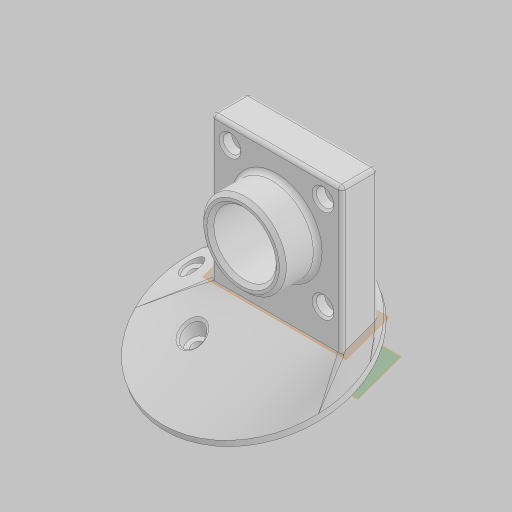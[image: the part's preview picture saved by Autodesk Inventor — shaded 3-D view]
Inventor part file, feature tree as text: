
AUTODESK INVENTOR PART (.ipt)
format: ipt  version: 2023.5 (Build 275446000, 446)  size: 464,384 bytes
history: native  units: in
note: dims shown in document units (in); Inventor stores cm internally (conversion verified against a paired STEP export)
features: extrude x7, hole x3, fillet x3, other x3, projected_geometry x3, plane x2, chamfer x2, loft x1, sketch x1, revolve x1
ambient origin geometry x8: Origin, YZ Plane, XZ Plane, XY Plane, X Axis, Y Axis, Z Axis, Center Point
bodies: Solid1 (feature_tree)
feature tree (26):
  extrude  "Extrusion1"  Depth=0.15in
  extrude  "Extrusion2"  Depth=0.15in TaperAngle=0.0deg
  plane  "Work Plane1"
  extrude  "Extrusion3"  Depth=0.15in
  loft  "Loft1"
  extrude  "Extrusion4"  Depth=0.15in
  hole  "Hole1"  [1 undecoded]
  extrude  "Extrusion5"  Depth=0.15in TaperAngle=0.0deg
  extrude  "Extrusion6"  TaperAngle=0.0deg  [1 undecoded]
  hole  "Hole2"  [1 undecoded]
  plane  "Work Plane2"
  hole  "Hole3"  [1 undecoded]
  fillet  "Fillet1"  Radius=0.3in
  chamfer  "Chamfer1"  Distance=1.1875in
  fillet  "Fillet2"  Radius=0.5in
  extrude  "Extrusion7"  Depth=0.15in
  fillet  "Fillet3"  Radius=1.3386in
  chamfer  "Chamfer2"  Distance=0.15in
  other  "Edges1"
  other  "Edges2"
  projected_geometry  "Projected Loop1"
  projected_geometry  "Projected Loop2"
  sketch  "Sketch11"  dims[d0=1.875in d1=0.525in d2=1.875in d3=0.0in d4=0.481in d5=1.875in d6=0.0in d7=0.6in d9=2.75in d10=0.1in d11=0.0in d12=0.0in d13=90.0deg d14=0.0in d15=90.0deg d16=1.6in d17=0.3in d18=0.0in d19=0.9in d20=0.75in d21=0.119in d22=0.25in d23=0.6871in d24=1.0in d25=0.8108in d26=1.1875in d27=0.5in d28=0.0in d29=0.1839in d30=1.3386in d31=0.15in d32=0.0in d33=0.094in d34=0.75in d35=0.251in d36=0.15in d37=0.6871in d38=1.0in d39=0.8108in d40=0.9792in d41=0.9792in d42=315.0deg d45=0.177in d46=0.75in d47=0.313in d48=0.45in d49=0.5635in d50=1.0in d51=0.8108in d52=0.05in d53=0.05in d54=0.125in d55=45.0deg d56=0.0625in d57=1.0in d58=1.0in d59=0.0in d60=0.25in d61=0.0312in d62=0.125in d63=45.0deg d64=0.2405in d65=90.0deg]
  other  "Srf1"
  revolve  "RevolutionSrf1"  [1 undecoded]
  projected_geometry  "Project Cut Edges1"
note: 5 required parameter values undecoded (feature->parameter linkage not recoverable at this tier; creation-order binding heuristic only, values carry confidence <= 0.55)